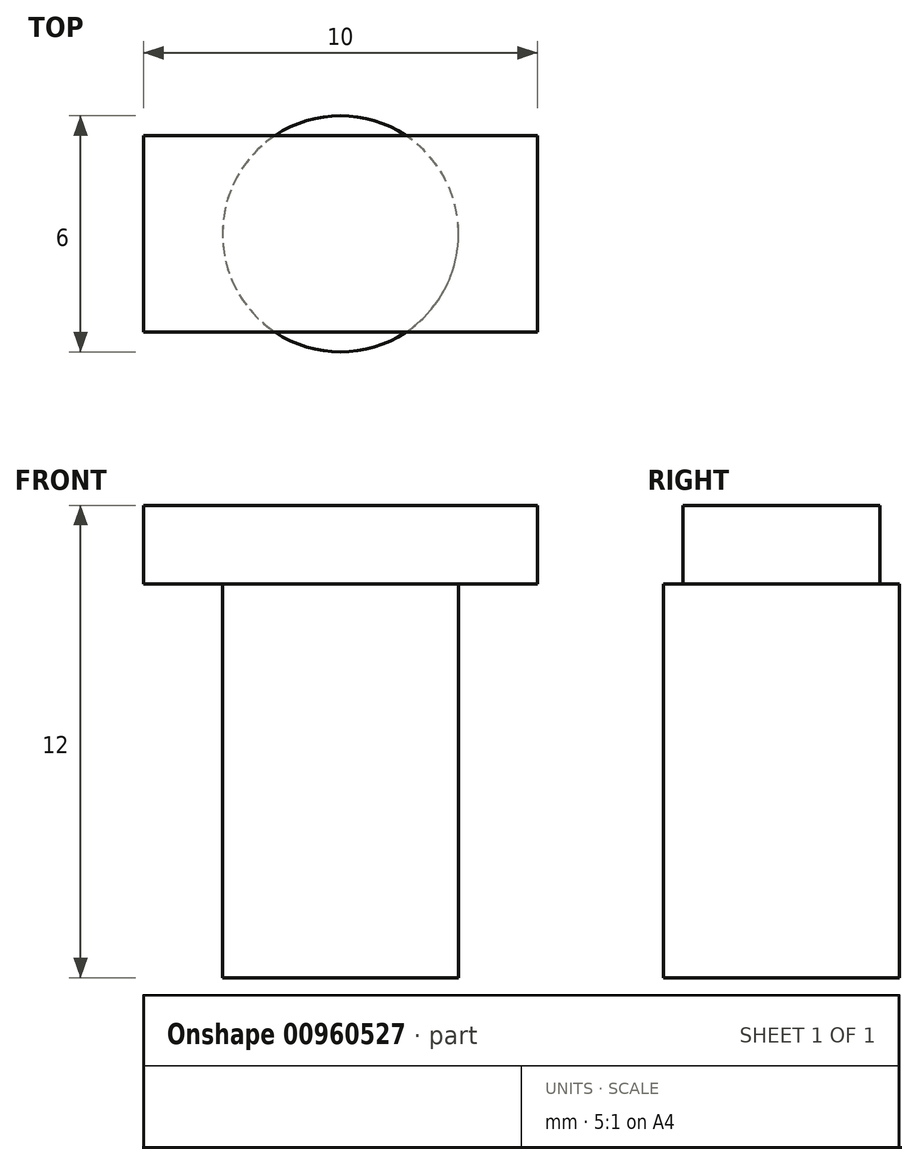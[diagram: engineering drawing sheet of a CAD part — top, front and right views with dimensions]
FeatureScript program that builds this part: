
annotation { "Feature Type Name" : "Feature", "Feature Type Description" : "" }
export const myFeature = defineFeature(function(context is Context, id is Id, definition is map)
    precondition{}
    {
        {
            var Q0;
            Q0=qCreatedBy(makeId("Front.planeOp"),FACE);
            var sketch = newSketch(context, id + "F0", { "sketchPlane" : qUnion([Q0])});
            skLineSegment(sketch, "E0.bottom", {"start": v(3, 0) * mm, "end": v(-3, 0) * mm});
            skLineSegment(sketch, "E0.top", {"start": v(3, 10) * mm, "end": v(-3, 10) * mm});
            skLineSegment(sketch, "E0.left", {"start": v(3, 0) * mm, "end": v(3, 10) * mm});
            skLineSegment(sketch, "E0.right", {"start": v(-3, 0) * mm, "end": v(-3, 10) * mm});
            skPoint(sketch, "E0.middle", {"position": v(0, 5) * mm});
            skLineSegment(sketch, "E1.bottom", {"start": v(5, 10) * mm, "end": v(-5, 10) * mm});
            skLineSegment(sketch, "E1.top", {"start": v(5, 12) * mm, "end": v(-5, 12) * mm});
            skLineSegment(sketch, "E1.left", {"start": v(5, 10) * mm, "end": v(5, 12) * mm});
            skLineSegment(sketch, "E1.right", {"start": v(-5, 10) * mm, "end": v(-5, 12) * mm});
            skPoint(sketch, "E1.middle", {"position": v(0, 11) * mm});
            skPoint(sketch, "E1.cornerSnap0", {"position": v(0, 10) * mm});
            skLineSegment(sketch, "E2", {"start": v(0, 10) * mm, "end": v(0, 0) * mm});
            skSolve(sketch);
        }
        {
            var Q0;
            {var subQ0=sQuery(id+"F0.wireOp",EDGE,"E0.right");Q0=makeQuery(id+"F0.imprint","IMPRINT",FACE,{"disambiguationData":[TD([[makeQuery(id+"F0.imprint","IMPRINT",EDGE,{"derivedFrom":subQ0}),-1.0]])]});}
            var Q1;
            Q1=sQuery(id+"F0.wireOp",EDGE,"E2");
            revolve(context, id + "F1", {"surfaceOperationType" : NewSurfaceOperationType.NEW, "entities" : qUnion([Q0]), "axis" : qUnion([Q1]), "revolveType" : RevolveType.FULL});
        }
        {
            var Q0;
            Q0=makeQuery(id+"F0.imprint","IMPRINT",FACE,{"disambiguationData":[TD([[makeQuery(id+"F0.imprint","IMPRINT",EDGE,{"derivedFrom":sQuery(id+"F0.wireOp",EDGE,"E1.top")}),1.0]])]});
            extrude(context, id + "F2", {"entities" : qUnion([Q0]), "operationType" : NewBodyOperationType.ADD, "depth" : 5 * mm, "offsetDistance" : 25 * mm, "symmetric" : true});
        }
    });
